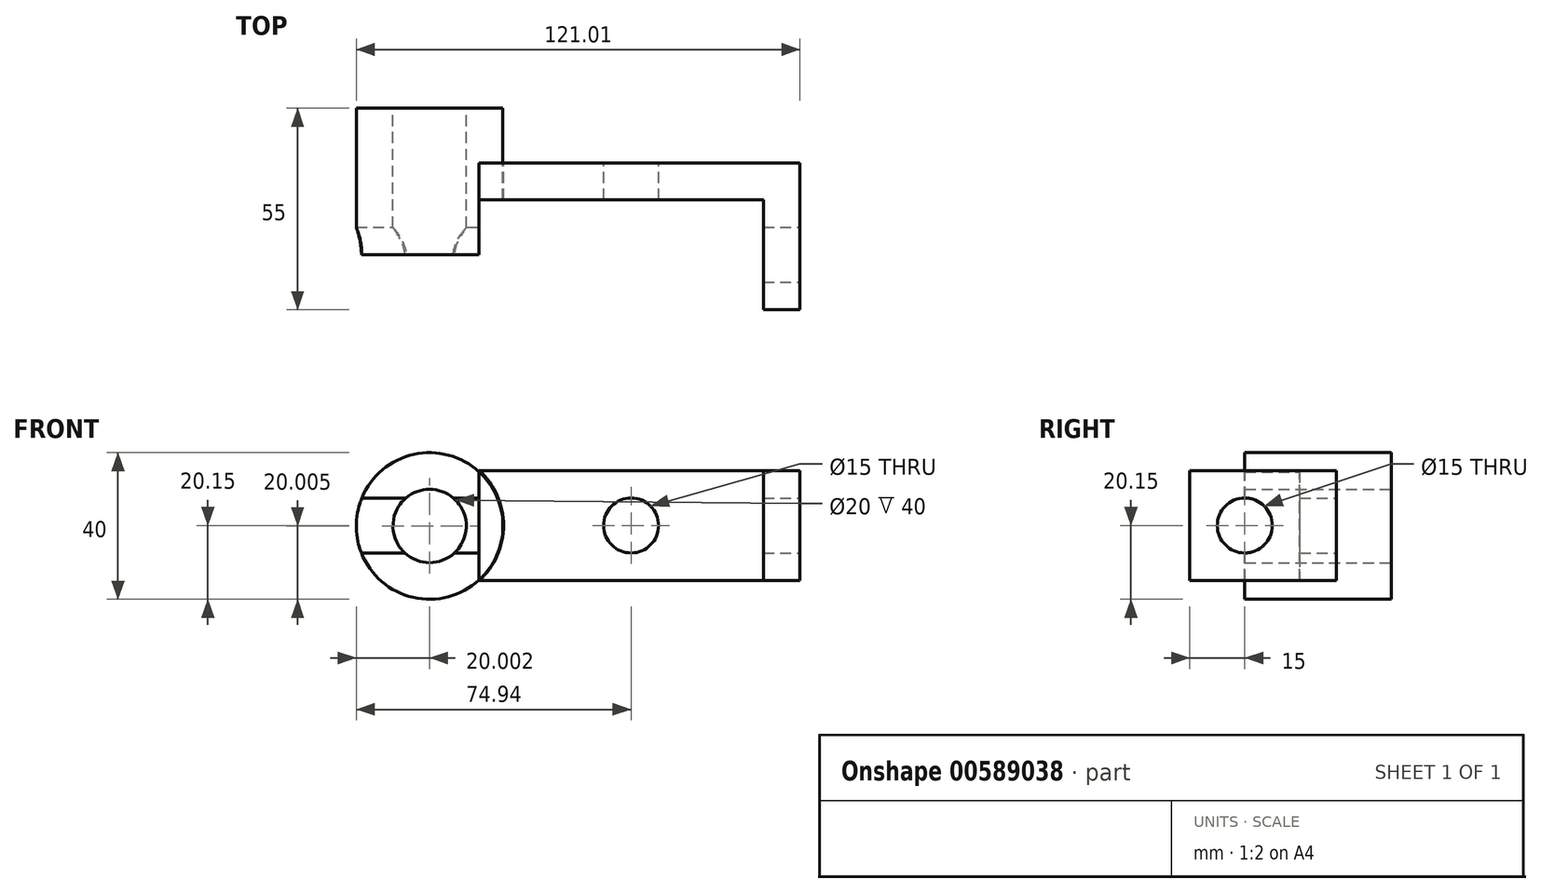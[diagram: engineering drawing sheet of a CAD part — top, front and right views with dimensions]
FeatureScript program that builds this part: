
annotation { "Feature Type Name" : "Feature", "Feature Type Description" : "" }
export const myFeature = defineFeature(function(context is Context, id is Id, definition is map)
    precondition{}
    {
        {
            var Q0;
            Q0=qCreatedBy(makeId("Front.planeOp"),FACE);
            var sketch = newSketch(context, id + "F0", { "sketchPlane" : qUnion([Q0])});
            skCircle(sketch, "E0", {"center": v(0.06, 19.85) * mm, "radius": 10 * mm});
            skCircle(sketch, "E1", {"center": v(0.06, 19.85) * mm, "radius": 20 * mm});
            skSolve(sketch);
        }
        {
            var Q0;
            Q0 = qSketchRegion(id + "F0", true);
            extrude(context, id + "F1", {"entities" : qUnion([Q0]), "depth" : 40 * mm, "offsetDistance" : 25 * mm});
        }
        {
            var Q0;
            Q0=makeQuery(id+"F1.opExtrude","CAP_FACE",FACE,{"disambiguationData":[OSD([sQuery(id+"F0.wireOp",EDGE,"E0"),sQuery(id+"F0.wireOp",EDGE,"E1")])],"isStart":true});
            cPlane(context, id + "F2", {"entities" : qUnion([Q0]), "cplaneType" : CPlaneType.OFFSET, "offset" : 15 * mm, "oppositeDirection" : true, "width" : 150 * mm, "height" : 150 * mm});
        }
        {
            var Q0;
            Q0=qCreatedBy(id+"F2.planeOp",FACE);
            var sketch = newSketch(context, id + "F3", { "sketchPlane" : qUnion([Q0])});
            skLineSegment(sketch, "E2", {"start": v(0, 20) * mm, "end": v(-101.07, 20) * mm, "construction": true});
            skLineSegment(sketch, "E3", {"start": v(-101.07, 20) * mm, "end": v(-101.07, 5) * mm});
            skLineSegment(sketch, "E4", {"start": v(-101.07, 20) * mm, "end": v(-101.07, 35) * mm});
            skLineSegment(sketch, "E5", {"start": v(-101.07, 5) * mm, "end": v(-13.5, 5) * mm});
            skLineSegment(sketch, "E6", {"start": v(-101.07, 35) * mm, "end": v(-13.12, 35) * mm});
            skCircle(sketch, "E7", {"center": v(0, 20) * mm, "radius": 20.23 * mm});
            skSolve(sketch);
        }
        {
            var Q0;
            {var subQ5=sQuery(id+"F3.wireOp",EDGE,"E3");Q0=makeQuery(id+"F3.imprint","IMPRINT",FACE,{"disambiguationData":[TD([[makeQuery(id+"F3.imprint","IMPRINT",EDGE,{"derivedFrom":subQ5}),1.0]])]});}
            extrude(context, id + "F4", {"entities" : qUnion([Q0]), "oppositeDirection" : true, "depth" : 40 * mm, "offsetDistance" : 25 * mm});
        }
        {
            var Q0;
            Q0=makeQuery(id+"F4.opExtrude","SWEPT_FACE",FACE,{"disambiguationData":[OSD([sQuery(id+"F3.wireOp",EDGE,"E6")])]});
            var sketch = newSketch(context, id + "F5", { "sketchPlane" : qUnion([Q0])});
            skLineSegment(sketch, "E8", {"start": v(101.07, -55) * mm, "end": v(91.07, -55) * mm});
            skLineSegment(sketch, "E9", {"start": v(91.07, -55) * mm, "end": v(91.07, -25) * mm});
            skLineSegment(sketch, "E10", {"start": v(91.07, -25) * mm, "end": v(13.58, -25) * mm});
            skLineSegment(sketch, "E11", {"start": v(13.58, -25) * mm, "end": v(13.58, -55) * mm});
            skLineSegment(sketch, "E12", {"start": v(13.58, -55) * mm, "end": v(91.07, -55) * mm});
            skSolve(sketch);
        }
        {
            var Q0;
            Q0=makeQuery(id+"F5.imprint","IMPRINT",FACE,{"disambiguationData":[TD([[makeQuery(id+"F5.imprint","IMPRINT",EDGE,{"derivedFrom":sQuery(id+"F5.wireOp",EDGE,"E9")}),1.0]])]});
            extrude(context, id + "F6", {"entities" : qUnion([Q0]), "operationType" : NewBodyOperationType.REMOVE, "endBound" : BoundingType.THROUGH_ALL, "oppositeDirection" : true, "depth" : 25 * mm, "offsetDistance" : 25 * mm});
        }
        {
            var Q0;
            Q0=makeQuery(id+"F4.opExtrude","CAP_FACE",FACE,{"disambiguationData":[OSD([sQuery(id+"F3.wireOp",EDGE,"E3"),sQuery(id+"F3.wireOp",EDGE,"E4"),sQuery(id+"F3.wireOp",EDGE,"E5"),sQuery(id+"F3.wireOp",EDGE,"E6"),sQuery(id+"F3.wireOp",EDGE,"E7")])],"isStart":true});
            var sketch = newSketch(context, id + "F7", { "sketchPlane" : qUnion([Q0])});
            skLineSegment(sketch, "E13", {"start": v(0, 20) * mm, "end": v(-55, 20) * mm, "construction": true});
            skCircle(sketch, "E14", {"center": v(-55, 20) * mm, "radius": 7.5 * mm});
            skSolve(sketch);
        }
        {
            var Q0;
            Q0=makeQuery(id+"F7.imprint","IMPRINT",FACE,{"disambiguationData":[TD([[makeQuery(id+"F7.imprint","IMPRINT",EDGE,{"derivedFrom":sQuery(id+"F7.wireOp",EDGE,"E14")}),1.0]])]});
            extrude(context, id + "F8", {"entities" : qUnion([Q0]), "operationType" : NewBodyOperationType.REMOVE, "endBound" : BoundingType.THROUGH_ALL, "oppositeDirection" : true, "depth" : 25 * mm, "offsetDistance" : 25 * mm});
        }
        {
            var Q0;
            Q0=makeQuery(id+"F4.opExtrude","SWEPT_FACE",FACE,{"disambiguationData":[OSD([sQuery(id+"F3.wireOp",EDGE,"E3"),sQuery(id+"F3.wireOp",EDGE,"E4")])]});
            var sketch = newSketch(context, id + "F9", { "sketchPlane" : qUnion([Q0])});
            skLineSegment(sketch, "E15", {"start": v(-55, 20) * mm, "end": v(-40, 20) * mm, "construction": true});
            skCircle(sketch, "E16", {"center": v(-40, 20) * mm, "radius": 7.5 * mm});
            skSolve(sketch);
        }
        {
            var Q0;
            Q0=makeQuery(id+"F9.imprint","IMPRINT",FACE,{"disambiguationData":[TD([[makeQuery(id+"F9.imprint","IMPRINT",EDGE,{"derivedFrom":sQuery(id+"F9.wireOp",EDGE,"E16")}),1.0]])]});
            extrude(context, id + "F10", {"entities" : qUnion([Q0]), "operationType" : NewBodyOperationType.REMOVE, "endBound" : BoundingType.THROUGH_ALL, "oppositeDirection" : true, "depth" : 25 * mm, "offsetDistance" : 25 * mm});
        }
    });
